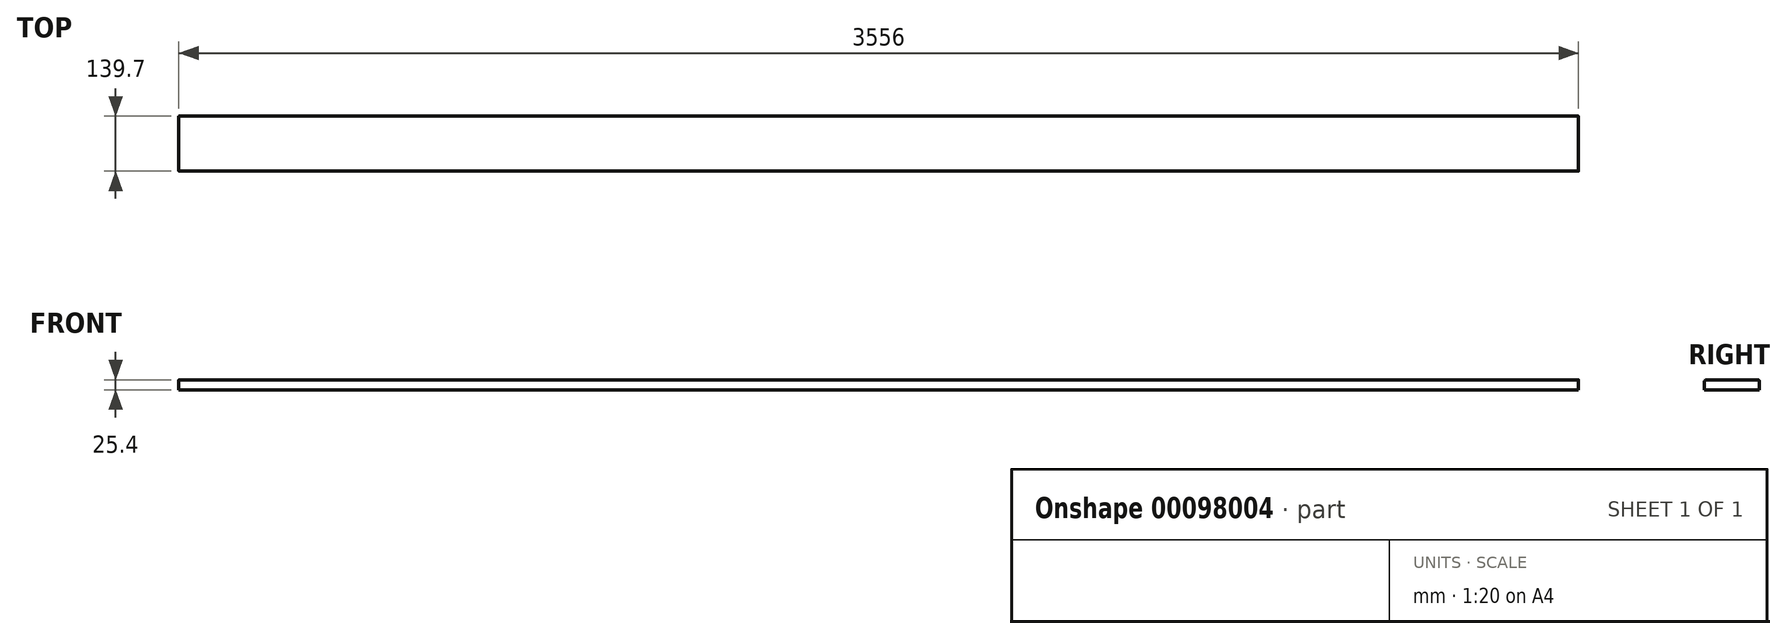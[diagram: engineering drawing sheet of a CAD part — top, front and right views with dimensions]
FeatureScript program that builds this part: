
annotation { "Feature Type Name" : "Feature", "Feature Type Description" : "" }
export const myFeature = defineFeature(function(context is Context, id is Id, definition is map)
    precondition{}
    {
        {
            var Q0;
            Q0=qCreatedBy(makeId("Top.planeOp"),FACE);
            var sketch = newSketch(context, id + "F0", { "sketchPlane" : qUnion([Q0])});
            skLineSegment(sketch, "E0.bottom", {"start": v(1778, 69.85) * mm, "end": v(-1778, 69.85) * mm});
            skLineSegment(sketch, "E0.top", {"start": v(1778, -69.85) * mm, "end": v(-1778, -69.85) * mm});
            skLineSegment(sketch, "E0.left", {"start": v(1778, 69.85) * mm, "end": v(1778, -69.85) * mm});
            skLineSegment(sketch, "E0.right", {"start": v(-1778, 69.85) * mm, "end": v(-1778, -69.85) * mm});
            skPoint(sketch, "E0.middle", {"position": v(0, 0) * mm});
            skSolve(sketch);
        }
        {
            var Q0;
            Q0=makeQuery(id+"F0.imprint","IMPRINT",FACE,{"disambiguationData":[TD([[makeQuery(id+"F0.imprint","IMPRINT",EDGE,{"derivedFrom":sQuery(id+"F0.wireOp",EDGE,"E0.bottom")}),1.0]])]});
            extrude(context, id + "F1", {"entities" : qUnion([Q0]), "depth" : 25.4 * mm});
        }
        {
            var Q0;
            Q0=makeQuery(id+"F1.opExtrude","CAP_EDGE",EDGE,{"disambiguationData":[OSD([sQuery(id+"F0.wireOp",EDGE,"E0.top")])],"isStart":false});
            var Q1;
            Q1=makeQuery(id+"F1.opExtrude","CAP_EDGE",EDGE,{"disambiguationData":[OSD([sQuery(id+"F0.wireOp",EDGE,"E0.bottom")])],"isStart":false});
            fillet(context, id + "F2", {"entities" : qUnion([Q0, Q1]), "radius" : 5.08 * mm, "tangentPropagation" : true, "allowEdgeOverflow" : false});
        }
    });
